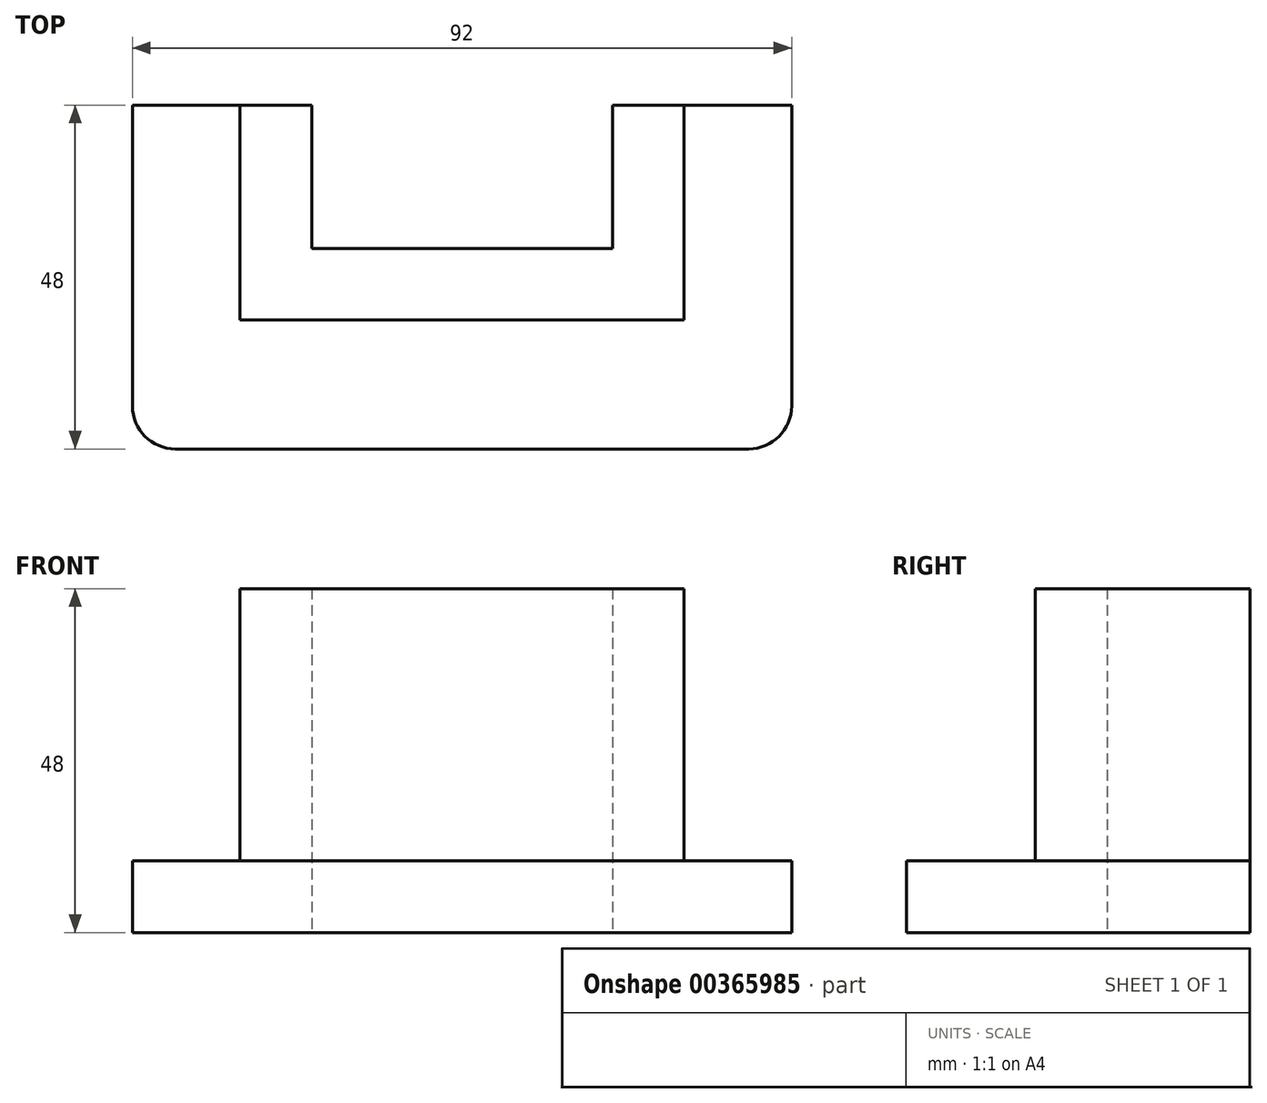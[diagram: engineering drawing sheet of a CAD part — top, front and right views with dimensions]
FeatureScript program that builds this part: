
annotation { "Feature Type Name" : "Feature", "Feature Type Description" : "" }
export const myFeature = defineFeature(function(context is Context, id is Id, definition is map)
    precondition{}
    {
        {
            var Q0;
            Q0=qCreatedBy(makeId("Top.planeOp"),FACE);
            var sketch = newSketch(context, id + "F0", { "sketchPlane" : qUnion([Q0])});
            skLineSegment(sketch, "E0", {"start": v(21, 10) * mm, "end": v(21, 30) * mm});
            skLineSegment(sketch, "E1", {"start": v(21, 30) * mm, "end": v(46, 30) * mm});
            skLineSegment(sketch, "E2", {"start": v(46, 30) * mm, "end": v(46, -18) * mm});
            skLineSegment(sketch, "E3", {"start": v(46, -18) * mm, "end": v(-46, -18) * mm});
            skLineSegment(sketch, "E4", {"start": v(-46, -18) * mm, "end": v(-46, 30) * mm});
            skLineSegment(sketch, "E5", {"start": v(-46, 30) * mm, "end": v(-21, 30) * mm});
            skLineSegment(sketch, "E6", {"start": v(-21, 30) * mm, "end": v(-21, 10) * mm});
            skLineSegment(sketch, "E7", {"start": v(-21, 10) * mm, "end": v(21, 10) * mm});
            skLineSegment(sketch, "E8", {"start": v(-46, 0) * mm, "end": v(46, 0) * mm});
            skLineSegment(sketch, "E9", {"start": v(-31, 30) * mm, "end": v(-31, 0) * mm});
            skLineSegment(sketch, "E10", {"start": v(31, 30) * mm, "end": v(31, 0) * mm});
            skSolve(sketch);
        }
        {
            var Q0;
            {var subQ4=sQuery(id+"F0.wireOp",EDGE,"E0");Q0=makeQuery(id+"F0.imprint","IMPRINT",FACE,{"disambiguationData":[TD([[makeQuery(id+"F0.imprint","IMPRINT",EDGE,{"derivedFrom":subQ4}),-1.0]])]});}
            extrude(context, id + "F1", {"entities" : qUnion([Q0]), "depth" : 48 * mm});
        }
        {
            var Q0;
            {var subQ4=sQuery(id+"F0.wireOp",EDGE,"E3");Q0=makeQuery(id+"F0.imprint","IMPRINT",FACE,{"disambiguationData":[TD([[makeQuery(id+"F0.imprint","IMPRINT",EDGE,{"derivedFrom":subQ4}),-1.0]])]});}
            var Q1;
            {var subQ3=sQuery(id+"F0.wireOp",EDGE,"E10");Q1=makeQuery(id+"F0.imprint","IMPRINT",FACE,{"disambiguationData":[TD([[makeQuery(id+"F0.imprint","IMPRINT",EDGE,{"derivedFrom":subQ3}),1.0]])]});}
            var Q2;
            {var subQ5=sQuery(id+"F0.wireOp",EDGE,"E9");Q2=makeQuery(id+"F0.imprint","IMPRINT",FACE,{"disambiguationData":[TD([[makeQuery(id+"F0.imprint","IMPRINT",EDGE,{"derivedFrom":subQ5}),-1.0]])]});}
            extrude(context, id + "F2", {"entities" : qUnion([Q0, Q1, Q2]), "operationType" : NewBodyOperationType.ADD, "depth" : 10 * mm});
        }
        {
            var Q0;
            Q0=makeQuery(id+"F2.opExtrude","SWEPT_EDGE",EDGE,{"disambiguationData":[OSD([sQuery(id+"F0.wireOp",EDGE,"E2"),sQuery(id+"F0.wireOp",EDGE,"E3")])]});
            var Q1;
            Q1=makeQuery(id+"F2.opExtrude","SWEPT_EDGE",EDGE,{"disambiguationData":[OSD([sQuery(id+"F0.wireOp",EDGE,"E3"),sQuery(id+"F0.wireOp",EDGE,"E4")])]});
            fillet(context, id + "F3", {"entities" : qUnion([Q0, Q1]), "radius" : 6 * mm, "tangentPropagation" : true, "allowEdgeOverflow" : false});
        }
    });
